# Revit family: КП-1
name_source: partatom
category: Арматура воздуховодов
units: mm (PartAtom-declared; Revit-internal decimal feet)

## family parameters
Всегда вертикально = Да
На основе рабочей плоскости = Нет
Общий = Нет
При загрузке вырезать с полостями = Нет
Размер круглого соединителя = Использовать диаметр
Тип детали = Присоединяется

## types (21) — shared parameters
00_20_Виробник = Вентс
00_20_Назва = Клапан протипожежний вогнезатримувальний
URL = https://vents.ua
Довжина = 350 мм
Изготовитель = Вентс
Класифікація навантаження = HVAC
Матеріал зони обслуговуваня = <По категории>
Матеріал корпусу = Сталь, гальванізована
Напруга = 230 В
Размещение привода (внутри) = Нет
Размещение привода (снаружи) = Да
Частота = 50 Гц
zero-valued in all types: Отметка по умолчанию

## per-type parameters (varying)
| type | A | A1 | A2 | A3 | An | B | B1 | B2 | B3 | Bn | Вага | Висота | Установлена потужність | Ширина |
| КП-1-200х200-2-ПВП230Т-СН | 200 мм | 220 мм | 240 мм | 100 мм | 210 мм | 200 мм | 220 мм | 240 мм | 110 мм | 210 мм | 6.20 кг | 240 мм | 7 В·А | 240 мм |
| КП-1-1000х1000-2-ПВП230Т-СН | 1000 мм | 1030 мм | 1060 мм | 500 мм | 1010 мм | 1000 мм | 1030 мм | 1060 мм | 515 мм | 1010 мм | 41.70 кг | 1060 мм | 11 В·А | 1060 мм |
| КП-1-250х200-2-ПВП230Т-СН | 250 мм | 270 мм | 290 мм | 125 мм | 260 мм | 200 мм | 220 мм | 240 мм | 110 мм | 210 мм | 6.80 кг | 290 мм | 10 В·А | 240 мм |
| КП-1-250х250-2-ПВП230Т-СН | 250 мм | 270 мм | 290 мм | 125 мм | 260 мм | 250 мм | 270 мм | 290 мм | 135 мм | 260 мм | 7.30 кг | 290 мм | 10 В·А | 290 мм |
| КП-1-300х200-2-ПВП230Т-СН | 300 мм | 320 мм | 340 мм | 150 мм | 310 мм | 200 мм | 220 мм | 240 мм | 110 мм | 210 мм | 7.30 кг | 340 мм | 10 В·А | 240 мм |
| КП-1-300х250-2-ПВП230Т-СН | 300 мм | 320 мм | 340 мм | 150 мм | 310 мм | 250 мм | 270 мм | 290 мм | 135 мм | 260 мм | 7.90 кг | 340 мм | 10 В·А | 290 мм |
| КП-1-300х300-2-ПВП230Т-СН | 300 мм | 320 мм | 340 мм | 150 мм | 310 мм | 300 мм | 320 мм | 340 мм | 160 мм | 310 мм | 8.50 кг | 340 мм | 10 В·А | 340 мм |
| КП-1-400х250-2-ПВП230Т-СН | 400 мм | 420 мм | 440 мм | 200 мм | 410 мм | 250 мм | 270 мм | 290 мм | 135 мм | 260 мм | 9.10 кг | 440 мм | 10 В·А | 290 мм |
| КП-1-400х300-2-ПВП230Т-СН | 400 мм | 420 мм | 440 мм | 200 мм | 410 мм | 300 мм | 320 мм | 340 мм | 160 мм | 310 мм | 9.80 кг | 440 мм | 10 В·А | 340 мм |
| КП-1-400х400-2-ПВП230Т-СН | 400 мм | 420 мм | 440 мм | 200 мм | 410 мм | 400 мм | 420 мм | 440 мм | 210 мм | 410 мм | 11.30 кг | 440 мм | 10 В·А | 440 мм |
| КП-1-500х300-2-ПВП230Т-СН | 500 мм | 520 мм | 540 мм | 250 мм | 510 мм | 300 мм | 320 мм | 340 мм | 160 мм | 310 мм | 10.70 кг | 540 мм | 10 В·А | 340 мм |
| КП-1-500х400-2-ПВП230Т-СН | 500 мм | 520 мм | 540 мм | 250 мм | 510 мм | 400 мм | 420 мм | 440 мм | 210 мм | 410 мм | 12.90 кг | 540 мм | 10 В·А | 440 мм |
| КП-1-500х500-2-ПВП230Т-СН | 500 мм | 530 мм | 560 мм | 250 мм | 510 мм | 500 мм | 530 мм | 560 мм | 265 мм | 510 мм | 16.60 кг | 560 мм | 10 В·А | 560 мм |
| КП-1-600х400-2-ПВП230Т-СН | 600 мм | 620 мм | 640 мм | 300 мм | 610 мм | 400 мм | 420 мм | 440 мм | 210 мм | 410 мм | 14.50 кг | 640 мм | 10 В·А | 440 мм |
| КП-1-600х500-2-ПВП230Т-СН | 600 мм | 630 мм | 660 мм | 300 мм | 610 мм | 500 мм | 530 мм | 560 мм | 265 мм | 510 мм | 18.40 кг | 660 мм | 11 В·А | 560 мм |
| КП-1-600х600-2-ПВП230Т-СН | 600 мм | 630 мм | 660 мм | 300 мм | 610 мм | 600 мм | 630 мм | 660 мм | 315 мм | 610 мм | 20.60 кг | 660 мм | 11 В·А | 660 мм |
| КП-1-800х500-2-ПВП230Т-СН | 800 мм | 830 мм | 860 мм | 400 мм | 810 мм | 500 мм | 530 мм | 560 мм | 265 мм | 510 мм | 22.30 кг | 860 мм | 11 В·А | 560 мм |
| КП-1-800х600-2-ПВП230Т-СН | 800 мм | 830 мм | 860 мм | 400 мм | 810 мм | 600 мм | 630 мм | 660 мм | 315 мм | 610 мм | 24.80 кг | 860 мм | 11 В·А | 660 мм |
| КП-1-800х800-2-ПВП230Т-СН | 800 мм | 830 мм | 860 мм | 400 мм | 810 мм | 800 мм | 830 мм | 860 мм | 415 мм | 810 мм | 30.10 кг | 860 мм | 11 В·А | 860 мм |
| КП-1-1000х600-2-ПВП230Т-СН | 1000 мм | 1030 мм | 1060 мм | 500 мм | 1010 мм | 600 мм | 630 мм | 660 мм | 315 мм | 610 мм | 29.00 кг | 1060 мм | 11 В·А | 660 мм |
| КП-1-1000х800-2-ПВП230Т-СН | 1000 мм | 1030 мм | 1060 мм | 500 мм | 1010 мм | 800 мм | 830 мм | 860 мм | 415 мм | 810 мм | 35.40 кг | 1060 мм | 11 В·А | 860 мм |

note: column(s) folded — value = type name in every type: 00_20_Тип

## geometry (parser evidence)
native form markers: Blend x4
no freeform markers — native parametric forms only
